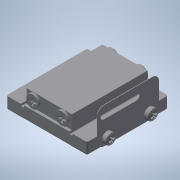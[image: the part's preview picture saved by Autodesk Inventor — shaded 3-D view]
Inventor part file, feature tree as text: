
AUTODESK INVENTOR PART (.ipt)
format: ipt  version: 2022 (Build 260153000, 153)  size: 1,573,376 bytes
history: native  units: in
note: dims shown in document units (in); Inventor stores cm internally (conversion verified against a paired STEP export)
features: plane x2, extrude x1, sketch x1
ambient origin geometry x8: Origin, YZ Plane, XZ Plane, XY Plane, X Axis, Y Axis, Z Axis, Center Point
bodies: Solid1 (feature_tree)
feature tree (4):
  extrude  "Extrusion1"  [1 undecoded]
  plane  "Work Plane1"
  plane  "Work Plane2"
  sketch  "Sketch1"  dims[d0=0.0in d1=0.0in]
note: 1 required parameter value undecoded (feature->parameter linkage not recoverable at this tier; creation-order binding heuristic only, values carry confidence <= 0.55)
